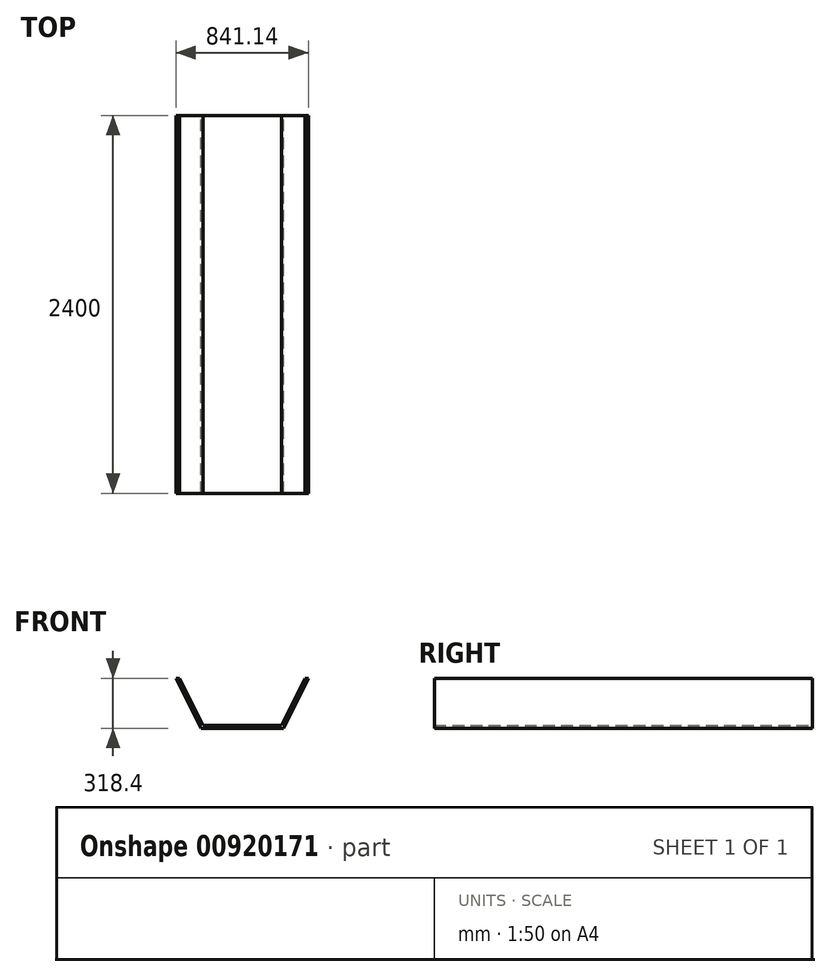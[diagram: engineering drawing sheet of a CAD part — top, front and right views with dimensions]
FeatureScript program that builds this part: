
annotation { "Feature Type Name" : "Feature", "Feature Type Description" : "" }
export const myFeature = defineFeature(function(context is Context, id is Id, definition is map)
    precondition{}
    {
        {
            var Q0;
            Q0=qCreatedBy(makeId("Front.planeOp"),FACE);
            var sketch = newSketch(context, id + "F0", { "sketchPlane" : qUnion([Q0])});
            skLineSegment(sketch, "E0.0", {"start": v(-398.21, 85.94) * mm, "end": v(-249.01, -212.46) * mm});
            skLineSegment(sketch, "E1.0", {"start": v(-249.01, -212.46) * mm, "end": v(249.01, -212.46) * mm});
            skLineSegment(sketch, "E2.0", {"start": v(398.21, 85.94) * mm, "end": v(249.01, -212.46) * mm});
            skLineSegment(sketch, "E3", {"start": v(-398.21, 85.94) * mm, "end": v(-418.21, 85.94) * mm});
            skLineSegment(sketch, "E4.0", {"start": v(-416.1, 77) * mm, "end": v(-266.9, -221.4) * mm});
            skLineSegment(sketch, "E5.0", {"start": v(-249.01, -232.46) * mm, "end": v(249.01, -232.46) * mm});
            skLineSegment(sketch, "E6.0", {"start": v(416.1, 77) * mm, "end": v(266.9, -221.4) * mm});
            skLineSegment(sketch, "E7", {"start": v(-418.21, 85.94) * mm, "end": v(-420.57, 85.94) * mm});
            skLineSegment(sketch, "E8", {"start": v(-416.1, 77) * mm, "end": v(-420.57, 85.94) * mm});
            skLineSegment(sketch, "E9", {"start": v(398.21, 85.94) * mm, "end": v(420.57, 85.94) * mm});
            skLineSegment(sketch, "E10", {"start": v(416.1, 77) * mm, "end": v(420.57, 85.94) * mm});
            skLineSegment(sketch, "E11", {"start": v(-266.9, -221.4) * mm, "end": v(-261.37, -232.46) * mm});
            skLineSegment(sketch, "E12", {"start": v(-249.01, -232.46) * mm, "end": v(-261.37, -232.46) * mm});
            skLineSegment(sketch, "E13", {"start": v(249.01, -232.46) * mm, "end": v(261.37, -232.46) * mm});
            skLineSegment(sketch, "E14", {"start": v(266.9, -221.4) * mm, "end": v(261.37, -232.46) * mm});
            skSolve(sketch);
        }
        {
            var Q0;
            Q0 = qSketchRegion(id + "F0", true);
            extrude(context, id + "F1", {"entities" : qUnion([Q0]), "depth" : 2400 * mm, "offsetDistance" : 25 * mm});
        }
    });
